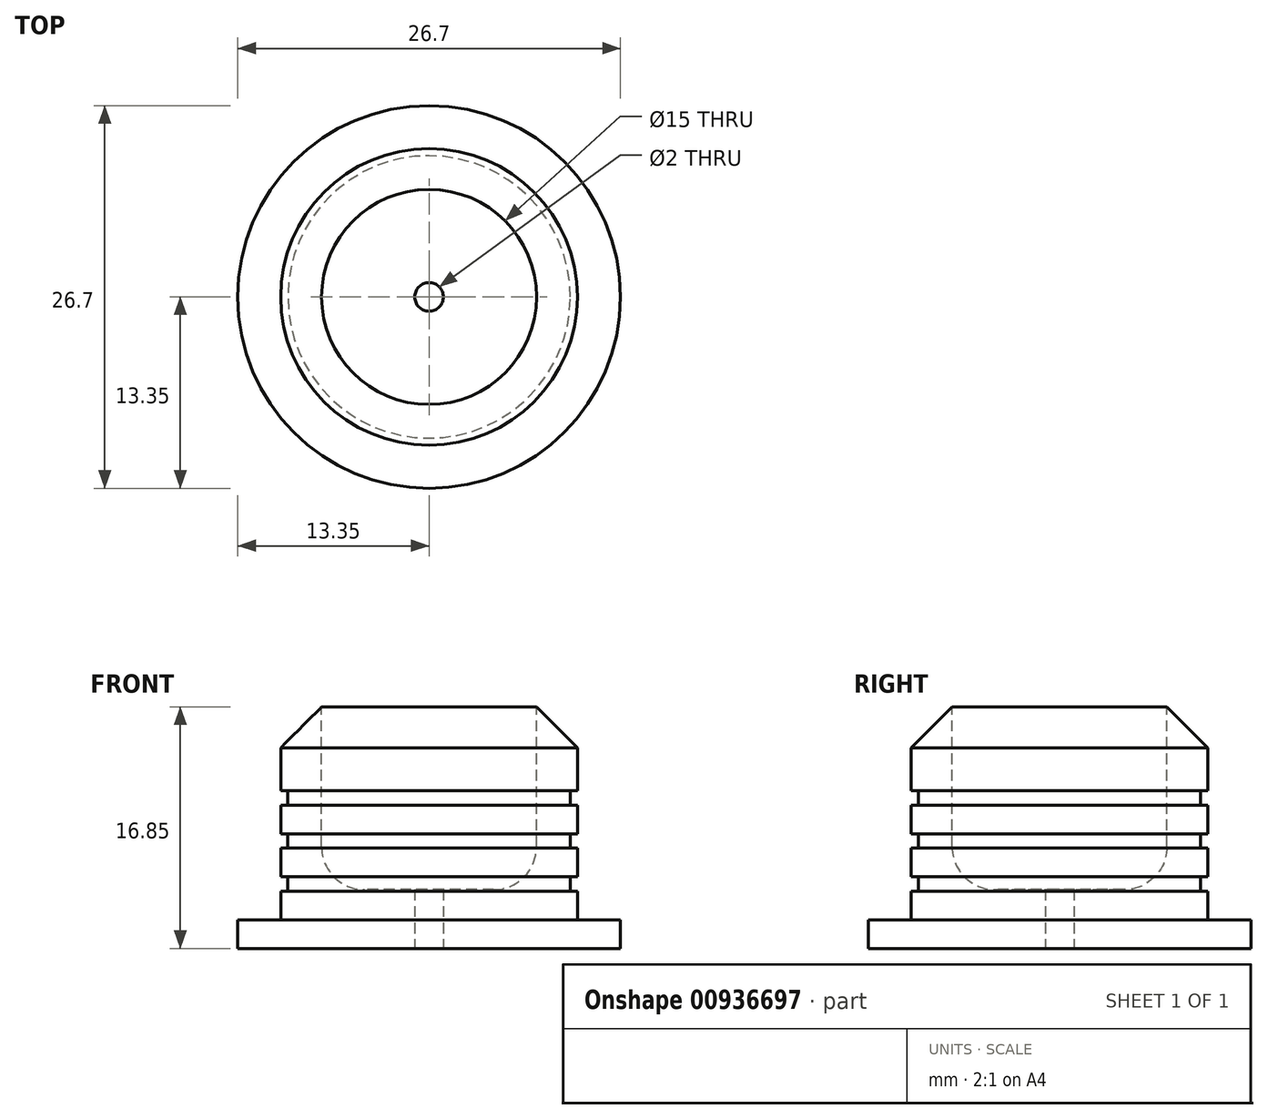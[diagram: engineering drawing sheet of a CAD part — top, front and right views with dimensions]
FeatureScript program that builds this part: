
annotation { "Feature Type Name" : "Feature", "Feature Type Description" : "" }
export const myFeature = defineFeature(function(context is Context, id is Id, definition is map)
    precondition{}
    {
        {
            var Q0;
            Q0=qCreatedBy(makeId("Front.planeOp"),FACE);
            var sketch = newSketch(context, id + "F0", { "sketchPlane" : qUnion([Q0])});
            skLineSegment(sketch, "E0", {"start": v(0, 0) * mm, "end": v(0, 24.32) * mm, "construction": true});
            skLineSegment(sketch, "E1", {"start": v(0, 0) * mm, "end": v(10.35, 0) * mm});
            skLineSegment(sketch, "E2", {"start": v(10.35, 2) * mm, "end": v(10.35, 4) * mm});
            skLineSegment(sketch, "E3", {"start": v(10.35, 17) * mm, "end": v(0, 17) * mm});
            skLineSegment(sketch, "E4", {"start": v(0, 17) * mm, "end": v(0, 0) * mm});
            skLineSegment(sketch, "E5", {"start": v(10.35, 4) * mm, "end": v(9.85, 4) * mm});
            skLineSegment(sketch, "E6", {"start": v(9.85, 4) * mm, "end": v(9.85, 5) * mm});
            skLineSegment(sketch, "E7", {"start": v(9.85, 5) * mm, "end": v(10.35, 5) * mm});
            skLineSegment(sketch, "E8", {"start": v(10.35, 0) * mm, "end": v(13.35, 0) * mm});
            skLineSegment(sketch, "E9", {"start": v(13.35, 0) * mm, "end": v(13.35, 2) * mm});
            skLineSegment(sketch, "E10", {"start": v(13.35, 2) * mm, "end": v(10.35, 2) * mm});
            skLineSegment(sketch, "E11.trimOffspring", {"start": v(10.35, 5) * mm, "end": v(10.35, 7) * mm});
            skLineSegment(sketch, "E12", {"start": v(10.35, 7) * mm, "end": v(9.85, 7) * mm});
            skLineSegment(sketch, "E13", {"start": v(9.85, 7) * mm, "end": v(9.85, 8) * mm});
            skLineSegment(sketch, "E14", {"start": v(9.85, 8) * mm, "end": v(10.35, 8) * mm});
            skLineSegment(sketch, "E15", {"start": v(10.35, 8) * mm, "end": v(10.35, 10) * mm});
            skLineSegment(sketch, "E16", {"start": v(10.35, 10) * mm, "end": v(9.85, 10) * mm});
            skLineSegment(sketch, "E17", {"start": v(9.85, 10) * mm, "end": v(9.85, 11) * mm});
            skLineSegment(sketch, "E18", {"start": v(9.85, 11) * mm, "end": v(10.35, 11) * mm});
            skLineSegment(sketch, "E19.trimOffspring", {"start": v(10.35, 11) * mm, "end": v(10.35, 17) * mm});
            skSolve(sketch);
        }
        {
            var Q0;
            Q0 = qSketchRegion(id + "F0", true);
            var Q1;
            Q1=sQuery(id+"F0.wireOp",EDGE,"E0");
            revolve(context, id + "F1", {"surfaceOperationType" : NewSurfaceOperationType.NEW, "entities" : qUnion([Q0]), "axis" : qUnion([Q1]), "revolveType" : RevolveType.FULL});
        }
        {
            var Q0;
            Q0=makeQuery(id+"F1.opRevolve","SWEPT_EDGE",EDGE,{"disambiguationData":[OSD([sQuery(id+"F0.wireOp",EDGE,"E3"),sQuery(id+"F0.wireOp",EDGE,"E19.trimOffspring")])]});
            chamfer(context, id + "F2", {"entities" : qUnion([Q0]), "width" : 3 * mm, "tangentPropagation" : true});
        }
        {
            var Q0;
            Q0=makeQuery(id+"F1.opRevolve","SWEPT_FACE",FACE,{"disambiguationData":[OSD([sQuery(id+"F0.wireOp",EDGE,"E3")])]});
            var sketch = newSketch(context, id + "F3", { "sketchPlane" : qUnion([Q0])});
            skCircle(sketch, "E20", {"center": v(0, 0) * mm, "radius": 7.5 * mm});
            skSolve(sketch);
        }
        {
            var Q0;
            Q0 = qSketchRegion(id + "F3", true);
            extrude(context, id + "F4", {"entities" : qUnion([Q0]), "operationType" : NewBodyOperationType.REMOVE, "oppositeDirection" : true, "depth" : 12.9 * mm, "offsetDistance" : 25 * mm});
        }
        {
            var Q0;
            Q0=makeQuery(id+"F4.boolean.opBoolean","COPY",EDGE,{"derivedFrom":makeQuery(id+"F4.opExtrude","CAP_EDGE",EDGE,{"disambiguationData":[OSD([sQuery(id+"F3.wireOp",EDGE,"E20")])],"isStart":false})});
            fillet(context, id + "F5", {"entities" : qUnion([Q0]), "radius" : 3 * mm, "tangentPropagation" : true, "allowEdgeOverflow" : false});
        }
        {
            var Q0;
            Q0=makeQuery(id+"F1.opRevolve","SWEPT_FACE",FACE,{"disambiguationData":[OSD([sQuery(id+"F0.wireOp",EDGE,"E1"),sQuery(id+"F0.wireOp",EDGE,"E8")])]});
            var sketch = newSketch(context, id + "F6", { "sketchPlane" : qUnion([Q0])});
            skCircle(sketch, "E21", {"center": v(0, 0) * mm, "radius": 1 * mm});
            skSolve(sketch);
        }
        {
            var Q0;
            Q0 = qSketchRegion(id + "F6", true);
            extrude(context, id + "F7", {"entities" : qUnion([Q0]), "operationType" : NewBodyOperationType.REMOVE, "oppositeDirection" : true, "depth" : 25 * mm, "offsetDistance" : 25 * mm});
        }
    });
